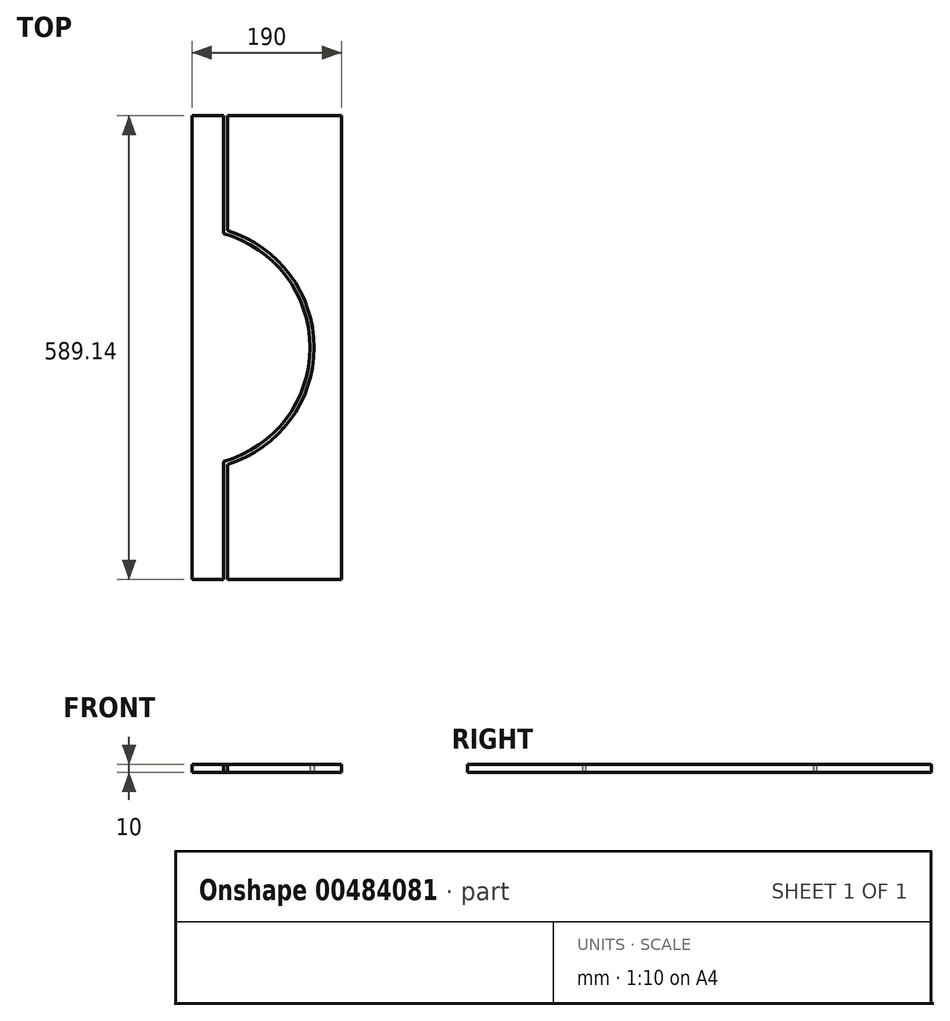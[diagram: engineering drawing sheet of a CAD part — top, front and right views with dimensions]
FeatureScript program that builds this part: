
annotation { "Feature Type Name" : "Feature", "Feature Type Description" : "" }
export const myFeature = defineFeature(function(context is Context, id is Id, definition is map)
    precondition{}
    {
        {
            var Q0;
            Q0=qCreatedBy(makeId("Top.planeOp"),FACE);
            var sketch = newSketch(context, id + "F0", { "sketchPlane" : qUnion([Q0])});
            skLineSegment(sketch, "E0", {"start": v(0, 0) * mm, "end": v(40, 0) * mm});
            skLineSegment(sketch, "E1", {"start": v(40, 0) * mm, "end": v(150, 0) * mm});
            skLineSegment(sketch, "E2", {"start": v(40, -144.57) * mm, "end": v(40, -294.57) * mm});
            skPoint(sketch, "E2.startSnap0", {"position": v(40, -135.44) * mm});
            skLineSegment(sketch, "E3", {"start": v(40, 144.57) * mm, "end": v(40, 294.57) * mm});
            skLineSegment(sketch, "E4", {"start": v(45, -294.57) * mm, "end": v(45, -148.32) * mm});
            skLineSegment(sketch, "E5", {"start": v(45, 294.57) * mm, "end": v(45, 148.32) * mm});
            skLineSegment(sketch, "E6", {"start": v(40, 294.57) * mm, "end": v(0, 294.57) * mm});
            skLineSegment(sketch, "E7", {"start": v(0, 294.57) * mm, "end": v(0, -294.57) * mm});
            skLineSegment(sketch, "E8", {"start": v(0, -294.57) * mm, "end": v(40, -294.57) * mm});
            skLineSegment(sketch, "E9", {"start": v(45, 294.57) * mm, "end": v(190, 294.57) * mm});
            skLineSegment(sketch, "E10", {"start": v(190, 294.57) * mm, "end": v(190, -294.57) * mm});
            skLineSegment(sketch, "E11", {"start": v(190, -294.57) * mm, "end": v(45, -294.57) * mm});
            skArc(sketch, "E12", {"start": v(40, -144.57) * mm, "mid": v(150, 0) * mm, "end": v(40, 144.57) * mm});
            skLineSegment(sketch, "E13", {"start": v(150, 0) * mm, "end": v(155, 0) * mm});
            skArc(sketch, "E14", {"start": v(45, -148.32) * mm, "mid": v(155, 0) * mm, "end": v(45, 148.32) * mm});
            skSolve(sketch);
        }
        {
            var Q0;
            Q0 = qSketchRegion(id + "F0", true);
            extrude(context, id + "F1", {"entities" : qUnion([Q0]), "depth" : 10 * mm, "offsetDistance" : 25 * mm});
        }
    });
